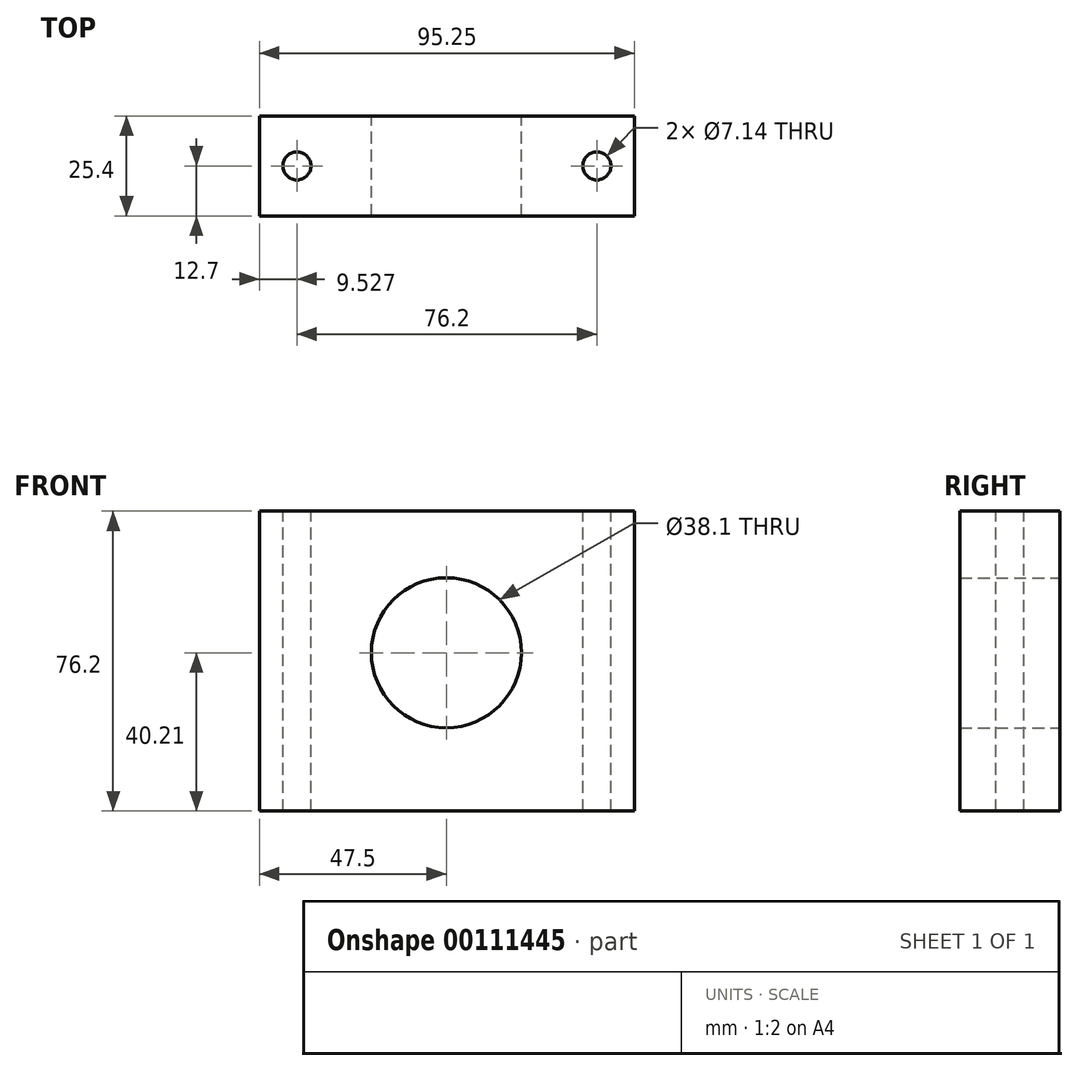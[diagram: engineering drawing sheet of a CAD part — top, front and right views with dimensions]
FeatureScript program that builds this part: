
annotation { "Feature Type Name" : "Feature", "Feature Type Description" : "" }
export const myFeature = defineFeature(function(context is Context, id is Id, definition is map)
    precondition{}
    {
        {
            var Q0;
            Q0=qCreatedBy(makeId("Front.planeOp"),FACE);
            var sketch = newSketch(context, id + "F0", { "sketchPlane" : qUnion([Q0])});
            skLineSegment(sketch, "E0.bottom", {"start": v(-47.5, 36) * mm, "end": v(47.75, 36) * mm});
            skLineSegment(sketch, "E0.top", {"start": v(-47.5, -40.2) * mm, "end": v(47.75, -40.2) * mm});
            skLineSegment(sketch, "E0.left", {"start": v(-47.5, 36) * mm, "end": v(-47.5, -40.2) * mm});
            skLineSegment(sketch, "E0.right", {"start": v(47.75, 36) * mm, "end": v(47.75, -40.2) * mm});
            skCircle(sketch, "E1", {"center": v(0, 0) * mm, "radius": 19.05 * mm});
            skSolve(sketch);
        }
        {
            var Q0;
            Q0=makeQuery(id+"F0.imprint","IMPRINT",FACE,{"disambiguationData":[TD([[makeQuery(id+"F0.imprint","IMPRINT",EDGE,{"derivedFrom":sQuery(id+"F0.wireOp",EDGE,"E0.bottom")}),-1.0]])]});
            extrude(context, id + "F1", {"entities" : qUnion([Q0]), "depth" : 25.4 * mm});
        }
        {
            var Q0;
            Q0=makeQuery(id+"F1.opExtrude","SWEPT_FACE",FACE,{"disambiguationData":[OSD([sQuery(id+"F0.wireOp",EDGE,"E0.bottom")])]});
            var sketch = newSketch(context, id + "F2", { "sketchPlane" : qUnion([Q0])});
            skCircle(sketch, "E2", {"center": v(-37.97, -12.7) * mm, "radius": 3.57 * mm});
            skCircle(sketch, "E3", {"center": v(38.23, -12.7) * mm, "radius": 3.57 * mm});
            skSolve(sketch);
        }
        {
            var Q0;
            Q0=makeQuery(id+"F2.imprint","IMPRINT",FACE,{"disambiguationData":[TD([[makeQuery(id+"F2.imprint","IMPRINT",EDGE,{"derivedFrom":sQuery(id+"F2.wireOp",EDGE,"E2")}),1.0]])]});
            var Q1;
            Q1=makeQuery(id+"F2.imprint","IMPRINT",FACE,{"disambiguationData":[TD([[makeQuery(id+"F2.imprint","IMPRINT",EDGE,{"derivedFrom":sQuery(id+"F2.wireOp",EDGE,"E3")}),1.0]])]});
            var Q2;
            Q2=sQuery(id+"F2.wireOp",EDGE,"E3");
            extrude(context, id + "F3", {"entities" : qUnion([Q0, Q1]), "operationType" : NewBodyOperationType.REMOVE, "surfaceEntities" : qUnion([Q2]), "endBound" : BoundingType.THROUGH_ALL, "oppositeDirection" : true, "depth" : 25.4 * mm});
        }
    });
